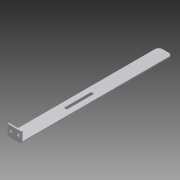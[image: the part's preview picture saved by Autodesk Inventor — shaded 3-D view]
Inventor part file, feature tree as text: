
AUTODESK INVENTOR PART (.ipt)
format: ipt  version: 2015 (Build 190159000, 159)  size: 130,560 bytes
history: native  units: mm
features: sketch x4, extrude x3, other x1, hole x1, fillet x1
ambient origin geometry x8: Origin, YZ Plane, XZ Plane, XY Plane, X Axis, Y Axis, Z Axis, Center Point
bodies: Body1 (feature_tree)
feature tree (10):
  other  "ソリッド1"
  extrude  "押し出し1"  Depth=15.0mm
  extrude  "押し出し2"  Depth=166.0mm
  extrude  "押し出し3"  Depth=1.5mm TaperAngle=0.0deg
  hole  "穴1"  [1 undecoded]
  fillet  "フィレット1"  Radius=30.0mm
  sketch  "スケッチ1"
  sketch  "スケッチ2"
  sketch  "スケッチ3"
  sketch  "スケッチ4"
note: 1 required parameter value undecoded (feature->parameter linkage not recoverable at this tier; creation-order binding heuristic only, values carry confidence <= 0.55)
